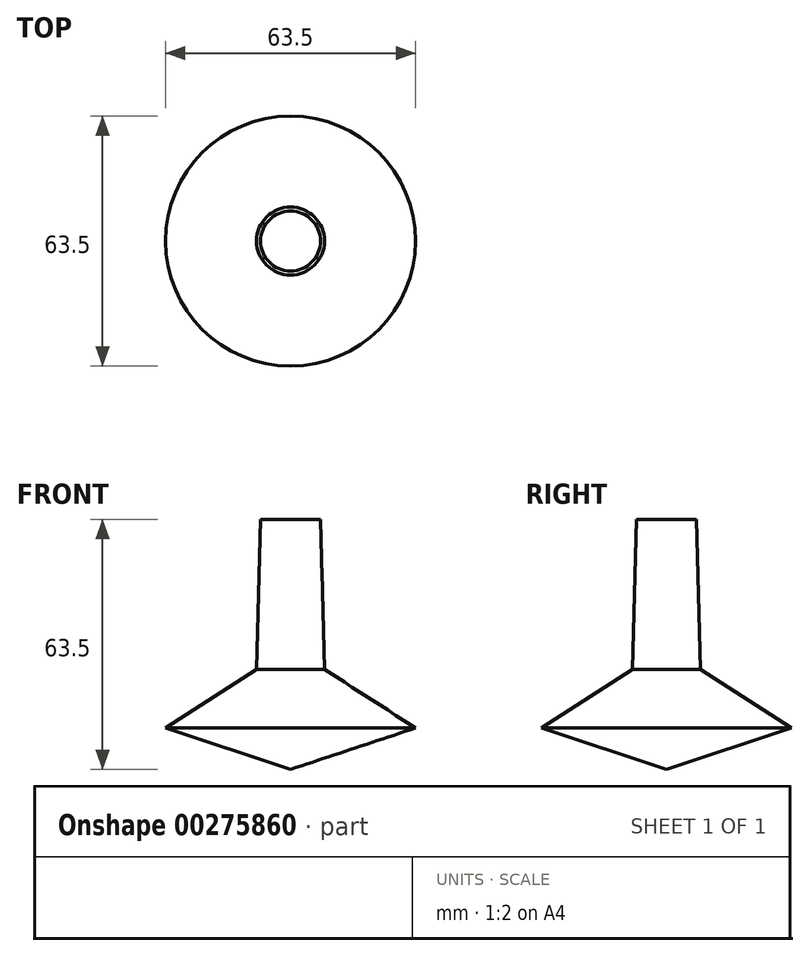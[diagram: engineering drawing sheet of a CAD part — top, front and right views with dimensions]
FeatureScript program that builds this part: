
annotation { "Feature Type Name" : "Feature", "Feature Type Description" : "" }
export const myFeature = defineFeature(function(context is Context, id is Id, definition is map)
    precondition{}
    {
        {
            var Q0;
            Q0=qCreatedBy(makeId("Front.planeOp"),FACE);
            var sketch = newSketch(context, id + "F0", { "sketchPlane" : qUnion([Q0])});
            skLineSegment(sketch, "E0", {"start": v(0, -44.1) * mm, "end": v(31.75, -33.57) * mm});
            skLineSegment(sketch, "E1", {"start": v(31.75, -33.57) * mm, "end": v(8.64, -18.7) * mm});
            skLineSegment(sketch, "E2", {"start": v(8.64, -18.7) * mm, "end": v(7.62, 19.4) * mm});
            skLineSegment(sketch, "E3", {"start": v(7.62, 19.4) * mm, "end": v(0, 19.4) * mm});
            skLineSegment(sketch, "E4", {"start": v(0, 19.4) * mm, "end": v(0, -44.1) * mm});
            skSolve(sketch);
        }
        {
            var Q0;
            Q0 = qSketchRegion(id + "F0", true);
            var Q1;
            Q1=sQuery(id+"F0.wireOp",EDGE,"E4");
            revolve(context, id + "F1", {"entities" : qUnion([Q0]), "axis" : qUnion([Q1]), "revolveType" : RevolveType.FULL});
        }
    });
